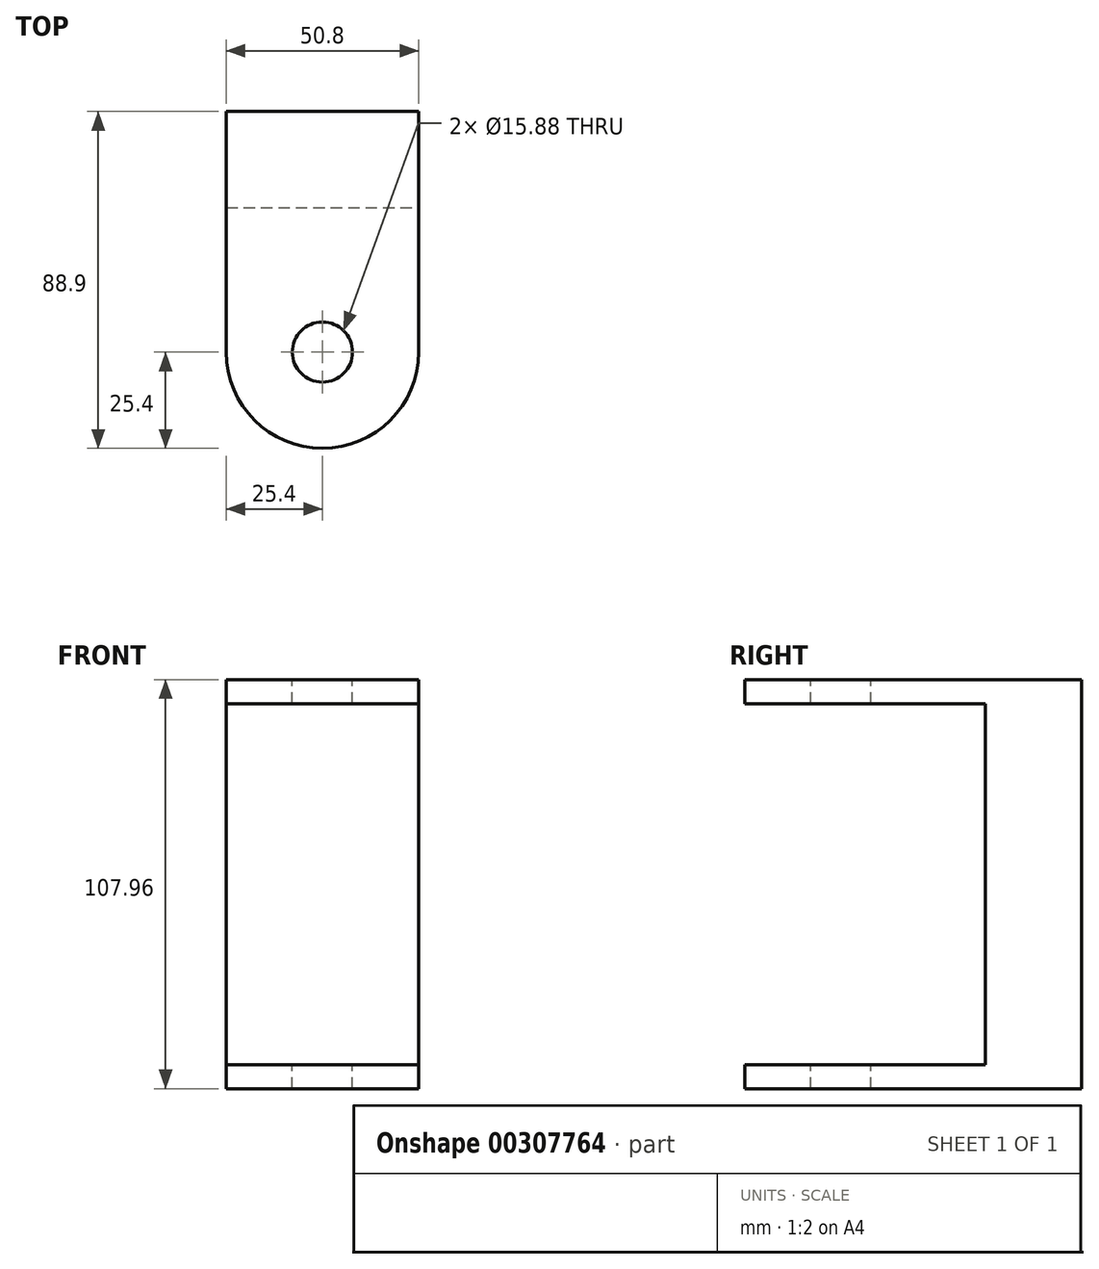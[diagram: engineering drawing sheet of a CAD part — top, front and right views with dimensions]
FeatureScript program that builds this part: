
annotation { "Feature Type Name" : "Feature", "Feature Type Description" : "" }
export const myFeature = defineFeature(function(context is Context, id is Id, definition is map)
    precondition{}
    {
        {
            var Q0;
            Q0=qCreatedBy(makeId("Top.planeOp"),FACE);
            var sketch = newSketch(context, id + "F0", { "sketchPlane" : qUnion([Q0])});
            skLineSegment(sketch, "E0.bottom", {"start": v(-25.4, 63.5) * mm, "end": v(25.4, 63.5) * mm});
            skLineSegment(sketch, "E0.top", {"start": v(-25.4, 0) * mm, "end": v(25.4, 0) * mm});
            skLineSegment(sketch, "E0.left", {"start": v(-25.4, 63.5) * mm, "end": v(-25.4, 0) * mm});
            skLineSegment(sketch, "E0.right", {"start": v(25.4, 63.5) * mm, "end": v(25.4, 0) * mm});
            skArc(sketch, "E1", {"start": v(-25.4, 0) * mm, "mid": v(0, -25.4) * mm, "end": v(25.4, 0) * mm});
            skSolve(sketch);
        }
        {
            var Q0;
            Q0 = qSketchRegion(id + "F0", true);
            extrude(context, id + "F1", {"entities" : qUnion([Q0]), "endBound" : BoundingType.SYMMETRIC, "depth" : 107.95 * mm});
        }
        {
            var Q0;
            Q0=makeQuery(id+"F1.opExtrude","SWEPT_FACE",FACE,{"disambiguationData":[OSD([sQuery(id+"F0.wireOp",EDGE,"E0.right")])]});
            var sketch = newSketch(context, id + "F2", { "sketchPlane" : qUnion([Q0])});
            skLineSegment(sketch, "E2.bottom", {"start": v(38.1, 47.62) * mm, "end": v(-25.4, 47.62) * mm});
            skLineSegment(sketch, "E2.top", {"start": v(38.1, -47.62) * mm, "end": v(-25.4, -47.62) * mm});
            skLineSegment(sketch, "E2.left", {"start": v(38.1, 47.62) * mm, "end": v(38.1, -47.62) * mm});
            skLineSegment(sketch, "E2.right", {"start": v(-25.4, 47.62) * mm, "end": v(-25.4, -47.62) * mm});
            skLineSegment(sketch, "E3", {"start": v(0, 0) * mm, "end": v(13.63, 0) * mm});
            skSolve(sketch);
        }
        {
            var Q0;
            {var subQ0=sQuery(id+"F2.wireOp",EDGE,"E2.right");Q0=makeQuery(id+"F2.imprint","IMPRINT",FACE,{"disambiguationData":[TD([[makeQuery(id+"F2.imprint","IMPRINT",EDGE,{"derivedFrom":subQ0}),1.0]])]});}
            var Q1;
            {var subQ4=sQuery(id+"F2.wireOp",EDGE,"E2.left");Q1=makeQuery(id+"F2.imprint","IMPRINT",FACE,{"disambiguationData":[TD([[makeQuery(id+"F2.imprint","IMPRINT",EDGE,{"derivedFrom":subQ4}),-1.0]])]});}
            extrude(context, id + "F3", {"entities" : qUnion([Q0, Q1]), "operationType" : NewBodyOperationType.REMOVE, "endBound" : BoundingType.THROUGH_ALL, "oppositeDirection" : true, "depth" : 25.4 * mm});
        }
        {
            var Q0;
            Q0=makeQuery(id+"F1.opExtrude","CAP_FACE",FACE,{"disambiguationData":[OSD([sQuery(id+"F0.wireOp",EDGE,"E0.bottom"),sQuery(id+"F0.wireOp",EDGE,"E0.left"),sQuery(id+"F0.wireOp",EDGE,"E0.right"),sQuery(id+"F0.wireOp",EDGE,"E1")])],"isStart":false});
            var sketch = newSketch(context, id + "F4", { "sketchPlane" : qUnion([Q0])});
            skCircle(sketch, "E4", {"center": v(0, 0) * mm, "radius": 7.94 * mm});
            skSolve(sketch);
        }
        {
            var Q0;
            Q0 = qSketchRegion(id + "F4", true);
            extrude(context, id + "F5", {"entities" : qUnion([Q0]), "operationType" : NewBodyOperationType.REMOVE, "endBound" : BoundingType.THROUGH_ALL, "oppositeDirection" : true, "depth" : 25.4 * mm});
        }
    });
